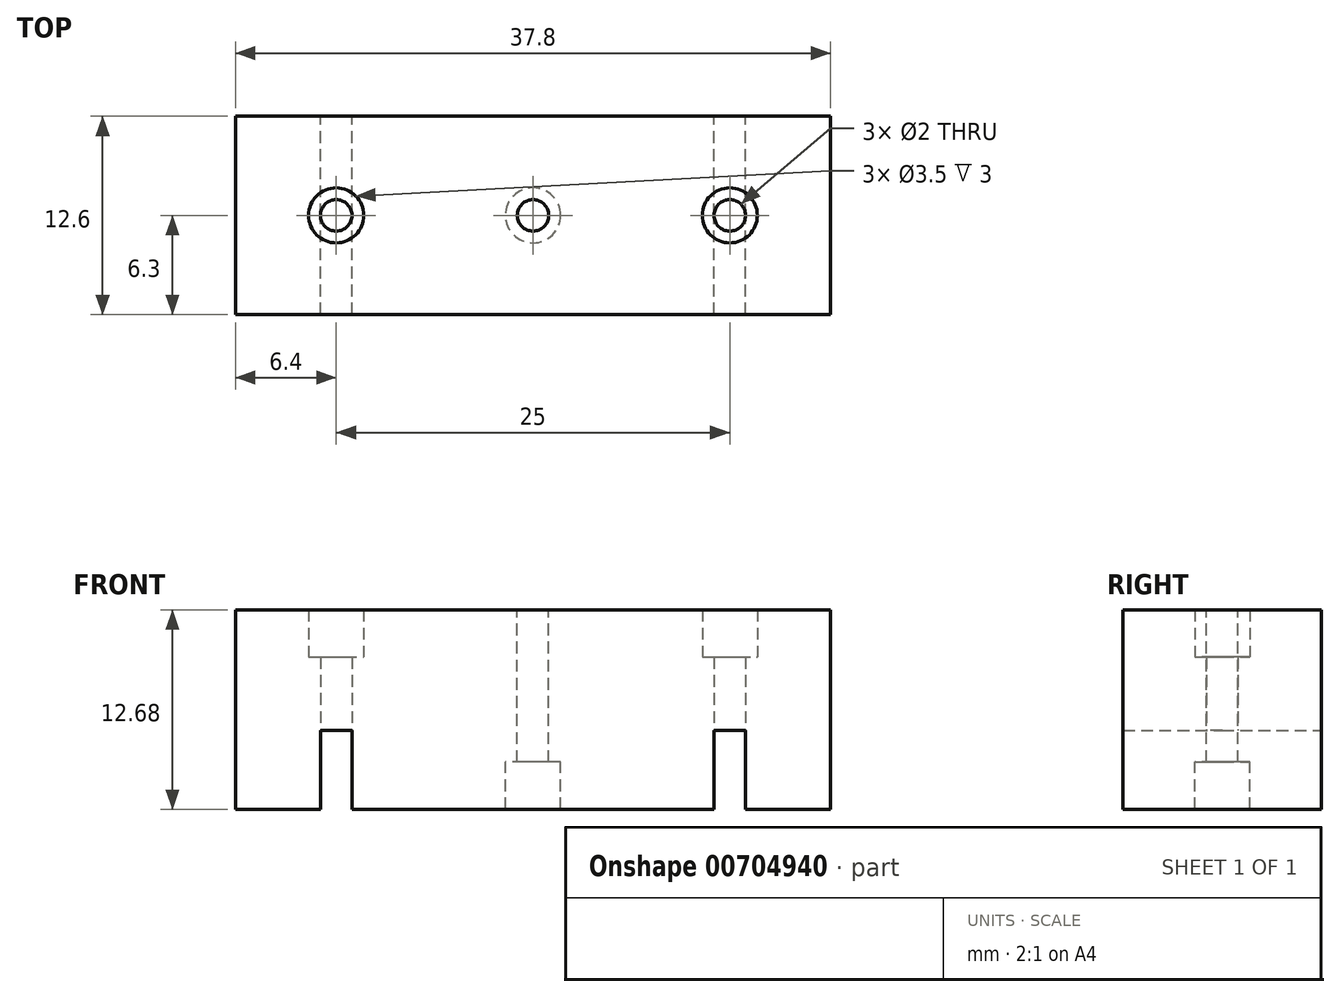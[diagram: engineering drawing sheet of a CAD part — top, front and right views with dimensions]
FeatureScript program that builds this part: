
annotation { "Feature Type Name" : "Feature", "Feature Type Description" : "" }
export const myFeature = defineFeature(function(context is Context, id is Id, definition is map)
    precondition{}
    {
        {
            var Q0;
            Q0=qCreatedBy(makeId("Front.planeOp"),FACE);
            var sketch = newSketch(context, id + "F0", { "sketchPlane" : qUnion([Q0])});
            skLineSegment(sketch, "E0.bottom", {"start": v(-18.9, 6.34) * mm, "end": v(18.9, 6.34) * mm});
            skLineSegment(sketch, "E0.top", {"start": v(-18.9, -6.34) * mm, "end": v(-13.5, -6.34) * mm});
            skLineSegment(sketch, "E0.left", {"start": v(-18.9, 6.34) * mm, "end": v(-18.9, -6.34) * mm});
            skLineSegment(sketch, "E0.right", {"start": v(18.9, 6.34) * mm, "end": v(18.9, -6.34) * mm});
            skPoint(sketch, "E0.middle", {"position": v(0, 0) * mm});
            skLineSegment(sketch, "E1", {"start": v(13.5, -6.34) * mm, "end": v(13.5, -1.34) * mm});
            skLineSegment(sketch, "E2", {"start": v(13.5, -1.34) * mm, "end": v(11.5, -1.34) * mm});
            skLineSegment(sketch, "E3", {"start": v(11.5, -1.34) * mm, "end": v(11.5, -6.34) * mm});
            skLineSegment(sketch, "E4.MirrorCS", {"start": v(-11.5, -1.34) * mm, "end": v(-11.5, -6.34) * mm});
            skLineSegment(sketch, "E5.MirrorCS", {"start": v(-13.5, -1.34) * mm, "end": v(-11.5, -1.34) * mm});
            skLineSegment(sketch, "E6.MirrorCS", {"start": v(-13.5, -6.34) * mm, "end": v(-13.5, -1.34) * mm});
            skLineSegment(sketch, "E7.trimOffspring", {"start": v(-11.5, -6.34) * mm, "end": v(11.5, -6.34) * mm});
            skLineSegment(sketch, "E8.trimOffspring", {"start": v(13.5, -6.34) * mm, "end": v(18.9, -6.34) * mm});
            skSolve(sketch);
        }
        {
            var Q0;
            Q0 = qSketchRegion(id + "F0", true);
            extrude(context, id + "F1", {"entities" : qUnion([Q0]), "depth" : 12.6 * mm, "offsetDistance" : 25 * mm});
        }
        {
            var Q0;
            Q0=makeQuery(id+"F1.opExtrude","SWEPT_FACE",FACE,{"disambiguationData":[OSD([sQuery(id+"F0.wireOp",EDGE,"E0.bottom")])]});
            var sketch = newSketch(context, id + "F2", { "sketchPlane" : qUnion([Q0])});
            skLineSegment(sketch, "E9", {"start": v(0, 11.93) * mm, "end": v(0, -17.08) * mm, "construction": true});
            skLineSegment(sketch, "E10", {"start": v(-18.9, -6.3) * mm, "end": v(23.41, -6.3) * mm, "construction": true});
            skCircle(sketch, "E11", {"center": v(0, -6.3) * mm, "radius": 1.82 * mm});
            skCircle(sketch, "E12", {"center": v(12.5, -6.3) * mm, "radius": 1.82 * mm});
            skCircle(sketch, "E13.MirrorC", {"center": v(-12.5, -6.3) * mm, "radius": 1.82 * mm});
            skSolve(sketch);
        }
        {
            var Q0;
            Q0=makeQuery(id+"F1.opExtrude","SWEPT_FACE",FACE,{"disambiguationData":[OSD([sQuery(id+"F0.wireOp",EDGE,"E7.trimOffspring")])]});
            var sketch = newSketch(context, id + "F3", { "sketchPlane" : qUnion([Q0])});
            skPoint(sketch, "E14", {"position": v(0, 6.3) * mm});
            skSolve(sketch);
        }
        {
            var Q0;
            Q0=sQuery(id+"F3.wireOp",VERTEX,"E14");
            var Q1;
            Q1=makeQuery(id+"F1.opExtrude","SWEPT_BODY",BODY,{"disambiguationData":[OSD([sQuery(id+"F0.wireOp",EDGE,"E0.bottom"),sQuery(id+"F0.wireOp",EDGE,"E0.top"),sQuery(id+"F0.wireOp",EDGE,"E0.left"),sQuery(id+"F0.wireOp",EDGE,"E0.right"),sQuery(id+"F0.wireOp",EDGE,"E1"),sQuery(id+"F0.wireOp",EDGE,"E2"),sQuery(id+"F0.wireOp",EDGE,"E3"),sQuery(id+"F0.wireOp",EDGE,"E4.MirrorCS"),sQuery(id+"F0.wireOp",EDGE,"E5.MirrorCS"),sQuery(id+"F0.wireOp",EDGE,"E6.MirrorCS"),sQuery(id+"F0.wireOp",EDGE,"E7.trimOffspring"),sQuery(id+"F0.wireOp",EDGE,"E8.trimOffspring")])]});
            hole(context, id + "F4", {"style" : HoleStyle.C_BORE, "endStyle" : HoleEndStyle.BLIND, "holeDiameter" : 2 * mm, "cBoreDiameter" : 3.5 * mm, "cBoreDepth" : 3 * mm, "majorDiameter" : 5 * mm, "holeDepth" : 38 * mm, "isTappedThrough" : true, "tappedDepth" : 12 * mm, "tapClearance" : 3, "locations" : qUnion([Q0]), "scope" : qUnion([Q1]), "startStyle" : HoleStartStyle.PART});
        }
        {
            var Q0;
            Q0=sQuery(id+"F2.wireOp",VERTEX,"E13.MirrorC.center");
            var Q1;
            Q1=sQuery(id+"F2.wireOp",VERTEX,"E12.center");
            var Q2;
            Q2=makeQuery(id+"F1.opExtrude","SWEPT_BODY",BODY,{"disambiguationData":[OSD([sQuery(id+"F0.wireOp",EDGE,"E0.bottom"),sQuery(id+"F0.wireOp",EDGE,"E0.top"),sQuery(id+"F0.wireOp",EDGE,"E0.left"),sQuery(id+"F0.wireOp",EDGE,"E0.right"),sQuery(id+"F0.wireOp",EDGE,"E1"),sQuery(id+"F0.wireOp",EDGE,"E2"),sQuery(id+"F0.wireOp",EDGE,"E3"),sQuery(id+"F0.wireOp",EDGE,"E4.MirrorCS"),sQuery(id+"F0.wireOp",EDGE,"E5.MirrorCS"),sQuery(id+"F0.wireOp",EDGE,"E6.MirrorCS"),sQuery(id+"F0.wireOp",EDGE,"E7.trimOffspring"),sQuery(id+"F0.wireOp",EDGE,"E8.trimOffspring")])]});
            hole(context, id + "F5", {"style" : HoleStyle.C_BORE, "endStyle" : HoleEndStyle.BLIND, "holeDiameter" : 2 * mm, "cBoreDiameter" : 3.5 * mm, "cBoreDepth" : 3 * mm, "majorDiameter" : 5 * mm, "holeDepth" : 38 * mm, "isTappedThrough" : true, "tappedDepth" : 12 * mm, "tapClearance" : 3, "locations" : qUnion([Q0, Q1]), "scope" : qUnion([Q2]), "startStyle" : HoleStartStyle.PART});
        }
    });
